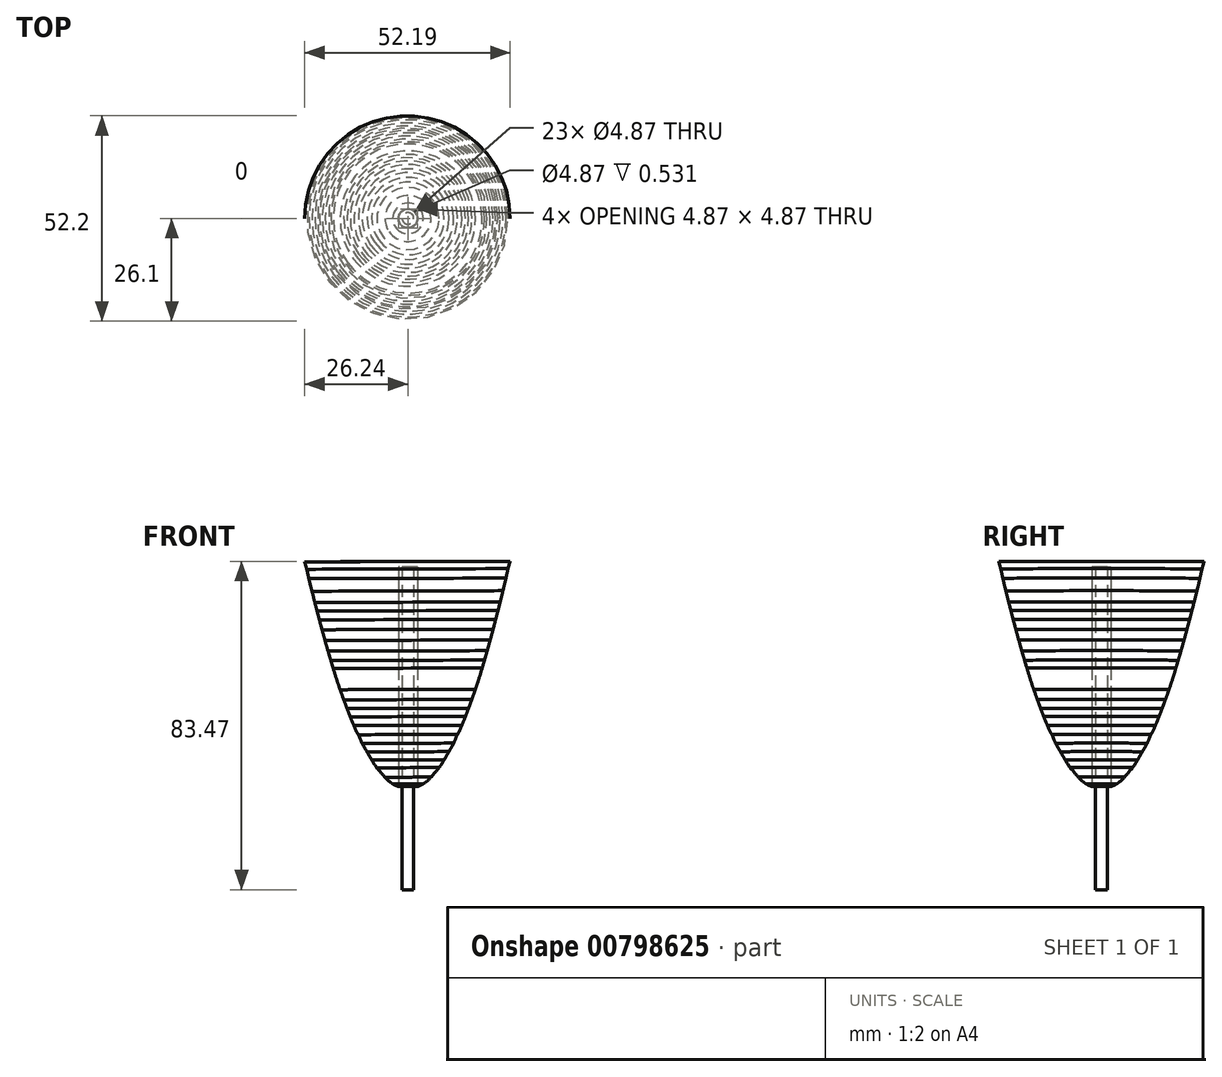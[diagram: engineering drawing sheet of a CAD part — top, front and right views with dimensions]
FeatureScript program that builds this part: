
annotation { "Feature Type Name" : "Feature", "Feature Type Description" : "" }
export const myFeature = defineFeature(function(context is Context, id is Id, definition is map)
    precondition{}
    {
        {
            var Q0;
            Q0=qCreatedBy(makeId("Front.planeOp"),FACE);
            var sketch = newSketch(context, id + "F0", { "sketchPlane" : qUnion([Q0])});
            skPoint(sketch, "E0", {"position": v(0.03, -0.02) * mm});
            skPoint(sketch, "E1", {"position": v(3.18, 1.13) * mm});
            skPoint(sketch, "E2", {"position": v(5.18, 2.5) * mm});
            skPoint(sketch, "E3", {"position": v(6.84, 4.37) * mm});
            skPoint(sketch, "E4", {"position": v(8.16, 5.94) * mm});
            skPoint(sketch, "E5", {"position": v(9.14, 7.52) * mm});
            skPoint(sketch, "E6", {"position": v(9.9, 8.84) * mm});
            skPoint(sketch, "E7", {"position": v(10.89, 10.54) * mm});
            skPoint(sketch, "E8", {"position": v(11.75, 12.1) * mm});
            skPoint(sketch, "E9", {"position": v(12.46, 13.83) * mm});
            skPoint(sketch, "E10", {"position": v(13.16, 15.1) * mm});
            skPoint(sketch, "E11", {"position": v(13.63, 16.27) * mm});
            skPoint(sketch, "E12", {"position": v(14.18, 17.52) * mm});
            skPoint(sketch, "E13", {"position": v(14.76, 19.04) * mm});
            skPoint(sketch, "E14", {"position": v(15.34, 20.55) * mm});
            skPoint(sketch, "E15", {"position": v(15.91, 22.07) * mm});
            skPoint(sketch, "E16", {"position": v(16.5, 23.66) * mm});
            skPoint(sketch, "E17", {"position": v(17, 25.39) * mm});
            skPoint(sketch, "E18", {"position": v(17.57, 26.83) * mm});
            skPoint(sketch, "E19", {"position": v(18.15, 28.78) * mm});
            skPoint(sketch, "E20", {"position": v(18.73, 30.87) * mm});
            skPoint(sketch, "E21", {"position": v(19.45, 32.97) * mm});
            skPoint(sketch, "E22", {"position": v(20.25, 35.58) * mm});
            skPoint(sketch, "E23", {"position": v(20.68, 37.74) * mm});
            skPoint(sketch, "E24", {"position": v(21.38, 39.85) * mm});
            skPoint(sketch, "E25", {"position": v(22, 42.1) * mm});
            skPoint(sketch, "E26", {"position": v(22.47, 44.2) * mm});
            skPoint(sketch, "E27", {"position": v(23.18, 47) * mm});
            skPoint(sketch, "E28", {"position": v(24.03, 50.12) * mm});
            skPoint(sketch, "E29", {"position": v(24.81, 53.4) * mm});
            skPoint(sketch, "E30", {"position": v(25.43, 56.2) * mm});
            skPoint(sketch, "E31", {"position": v(25.43, 58.07) * mm});
            skFitSpline(sketch, "E32", {"points": [v(0.03, -0.02) * mm, v(3.18, 1.13) * mm, v(5.18, 2.5) * mm, v(6.84, 4.37) * mm, v(8.16, 5.94) * mm, v(9.14, 7.52) * mm, v(9.9, 8.84) * mm, v(10.89, 10.54) * mm, v(11.75, 12.1) * mm, v(12.46, 13.83) * mm, v(13.16, 15.1) * mm, v(13.63, 16.27) * mm, v(14.18, 17.52) * mm, v(14.76, 19.04) * mm, v(15.34, 20.55) * mm, v(17.57, 26.83) * mm, v(19.45, 32.97) * mm, v(21.38, 39.85) * mm, v(24.81, 53.4) * mm, v(25.43, 56.2) * mm, v(25.95, 58.07) * mm], "startDerivative": vector(61.74, 19.66) * mm, "endDerivative": vector(13.33, 46) * mm});
            skLineSegment(sketch, "E33", {"start": v(25.95, 58.07) * mm, "end": v(-0.15, 58.07) * mm});
            skLineSegment(sketch, "E34", {"start": v(-0.15, 58.07) * mm, "end": v(0.03, -0.02) * mm});
            skLineSegment(sketch, "E35", {"start": v(19.45, 32.97) * mm, "end": v(-0.07, 32.97) * mm});
            skLineSegment(sketch, "E36", {"start": v(25.43, 56.2) * mm, "end": v(-0.14, 56.12) * mm});
            skLineSegment(sketch, "E37", {"start": v(23.97, 45.58) * mm, "end": v(-6.54, 45.48) * mm});
            skLineSegment(sketch, "E38", {"start": v(-4.68, 53.8) * mm, "end": v(34.04, 53.8) * mm});
            skLineSegment(sketch, "E39", {"start": v(-7.24, 50.6) * mm, "end": v(41.15, 50.6) * mm});
            skLineSegment(sketch, "E40", {"start": v(-7.24, 47.74) * mm, "end": v(38.8, 47.74) * mm});
            skLineSegment(sketch, "E41", {"start": v(-6.54, 43.31) * mm, "end": v(33.08, 43.31) * mm});
            skLineSegment(sketch, "E42", {"start": v(-6.61, 40.8) * mm, "end": v(35.36, 40.8) * mm});
            skLineSegment(sketch, "E43", {"start": v(-6.34, 38.08) * mm, "end": v(33.86, 38.08) * mm});
            skLineSegment(sketch, "E44", {"start": v(-4.24, 35.28) * mm, "end": v(35.36, 35.4) * mm});
            skLineSegment(sketch, "E45", {"start": v(-4.66, 30.97) * mm, "end": v(35.36, 30.97) * mm});
            skLineSegment(sketch, "E46", {"start": v(-4.61, 28.25) * mm, "end": v(32.86, 28.25) * mm});
            skLineSegment(sketch, "E47", {"start": v(-4.44, 25.54) * mm, "end": v(32.3, 25.54) * mm});
            skLineSegment(sketch, "E48", {"start": v(-4.61, 22.96) * mm, "end": v(29.5, 22.96) * mm});
            skLineSegment(sketch, "E49", {"start": v(-4.36, 20.74) * mm, "end": v(30.66, 20.74) * mm});
            skLineSegment(sketch, "E50", {"start": v(-4.32, 18.64) * mm, "end": v(26.14, 18.64) * mm});
            skLineSegment(sketch, "E51", {"start": v(-4.53, 16.42) * mm, "end": v(28.75, 16.42) * mm});
            skLineSegment(sketch, "E52", {"start": v(-4.37, 14.08) * mm, "end": v(25.46, 14.08) * mm});
            skLineSegment(sketch, "E53", {"start": v(-4.32, 11.86) * mm, "end": v(28.46, 11.86) * mm});
            skLineSegment(sketch, "E54", {"start": v(-4.25, 9.7) * mm, "end": v(25.28, 9.7) * mm});
            skLineSegment(sketch, "E55", {"start": v(-4.22, 7.66) * mm, "end": v(30.42, 7.66) * mm});
            skLineSegment(sketch, "E56", {"start": v(-4.18, 5.62) * mm, "end": v(24.54, 5.7) * mm});
            skLineSegment(sketch, "E57", {"start": v(-4.14, 3.23) * mm, "end": v(12.44, 3.23) * mm});
            skLineSegment(sketch, "E58", {"start": v(-4.34, 1.53) * mm, "end": v(8.85, 1.53) * mm});
            skSolve(sketch);
        }
        {
            var Q0;
            Q0=makeQuery(id+"F0.imprint","IMPRINT",FACE,{"disambiguationData":[TD([[makeQuery(id+"F0.imprint","IMPRINT",EDGE,{"derivedFrom":sQuery(id+"F0.wireOp",EDGE,"E32")}),1.0]])]});
            var Q1;
            Q1=sQuery(id+"F0.wireOp",EDGE,"E34");
            revolve(context, id + "F1", {"surfaceOperationType" : NewSurfaceOperationType.NEW, "entities" : qUnion([Q0]), "axis" : qUnion([Q1]), "revolveType" : RevolveType.FULL});
        }
        {
            var Q0;
            {var subQ0=sQuery(id+"F0.wireOp",EDGE,"E35");Q0=makeQuery(id+"F0.imprint","IMPRINT",FACE,{"disambiguationData":[TD([[makeQuery(id+"F0.imprint","IMPRINT",EDGE,{"derivedFrom":subQ0}),1.0]])]});}
            var Q1;
            Q1=sQuery(id+"F0.wireOp",EDGE,"E34");
            revolve(context, id + "F2", {"surfaceOperationType" : NewSurfaceOperationType.NEW, "entities" : qUnion([Q0]), "axis" : qUnion([Q1]), "revolveType" : RevolveType.FULL});
        }
        {
            var Q0;
            {var subQ0=sQuery(id+"F0.wireOp",EDGE,"E35");Q0=makeQuery(id+"F0.imprint","IMPRINT",FACE,{"disambiguationData":[TD([[makeQuery(id+"F0.imprint","IMPRINT",EDGE,{"derivedFrom":subQ0}),-1.0]])]});}
            var Q1;
            Q1=sQuery(id+"F0.wireOp",EDGE,"E34");
            revolve(context, id + "F3", {"surfaceOperationType" : NewSurfaceOperationType.NEW, "entities" : qUnion([Q0]), "axis" : qUnion([Q1]), "revolveType" : RevolveType.FULL});
        }
        {
            var Q0;
            {var subQ0=sQuery(id+"F0.wireOp",EDGE,"E36");Q0=makeQuery(id+"F0.imprint","IMPRINT",FACE,{"disambiguationData":[TD([[makeQuery(id+"F0.imprint","IMPRINT",EDGE,{"derivedFrom":subQ0}),1.0]])]});}
            var Q1;
            Q1=sQuery(id+"F0.wireOp",EDGE,"E34");
            revolve(context, id + "F4", {"surfaceOperationType" : NewSurfaceOperationType.NEW, "entities" : qUnion([Q0]), "axis" : qUnion([Q1]), "revolveType" : RevolveType.FULL});
        }
        {
            var Q0;
            {var subQ0=sQuery(id+"F0.wireOp",EDGE,"E33");Q0=makeQuery(id+"F0.imprint","IMPRINT",FACE,{"disambiguationData":[TD([[makeQuery(id+"F0.imprint","IMPRINT",EDGE,{"derivedFrom":subQ0}),1.0]])]});}
            var Q1;
            Q1=sQuery(id+"F0.wireOp",EDGE,"E34");
            revolve(context, id + "F5", {"surfaceOperationType" : NewSurfaceOperationType.NEW, "entities" : qUnion([Q0]), "axis" : qUnion([Q1]), "revolveType" : RevolveType.FULL});
        }
        {
            var Q0;
            {var subQ0=sQuery(id+"F0.wireOp",EDGE,"E39");var subQ1=sQuery(id+"F0.wireOp",EDGE,"E32");var subQ2=makeQuery(id+"F0.imprint","INTERSECT",VERTEX,{"derivedFrom":[subQ1,subQ0]});Q0=makeQuery(id+"F0.imprint","IMPRINT",FACE,{"disambiguationData":[TD([[makeQuery(id+"F0.imprint","IMPRINT",EDGE,{"disambiguationData":[TD([[subQ2,-1.0]])],"derivedFrom":subQ1}),1.0]])]});}
            var Q1;
            Q1=sQuery(id+"F0.wireOp",EDGE,"E34");
            revolve(context, id + "F6", {"surfaceOperationType" : NewSurfaceOperationType.NEW, "entities" : qUnion([Q0]), "axis" : qUnion([Q1]), "revolveType" : RevolveType.FULL});
        }
        {
            var Q0;
            {var subQ0=sQuery(id+"F0.wireOp",EDGE,"E40");var subQ1=sQuery(id+"F0.wireOp",EDGE,"E32");var subQ2=makeQuery(id+"F0.imprint","INTERSECT",VERTEX,{"derivedFrom":[subQ1,subQ0]});Q0=makeQuery(id+"F0.imprint","IMPRINT",FACE,{"disambiguationData":[TD([[makeQuery(id+"F0.imprint","IMPRINT",EDGE,{"disambiguationData":[TD([[subQ2,-1.0]])],"derivedFrom":subQ1}),1.0]])]});}
            var Q1;
            Q1=sQuery(id+"F0.wireOp",EDGE,"E34");
            revolve(context, id + "F7", {"surfaceOperationType" : NewSurfaceOperationType.NEW, "entities" : qUnion([Q0]), "axis" : qUnion([Q1]), "revolveType" : RevolveType.FULL});
        }
        {
            var Q0;
            {var subQ0=sQuery(id+"F0.wireOp",EDGE,"E37");var subQ1=sQuery(id+"F0.wireOp",EDGE,"E32");var subQ2=makeQuery(id+"F0.imprint","INTERSECT",VERTEX,{"derivedFrom":[subQ1,subQ0]});Q0=makeQuery(id+"F0.imprint","IMPRINT",FACE,{"disambiguationData":[TD([[makeQuery(id+"F0.imprint","IMPRINT",EDGE,{"disambiguationData":[TD([[subQ2,-1.0]])],"derivedFrom":subQ1}),1.0]])]});}
            var Q1;
            Q1=sQuery(id+"F0.wireOp",EDGE,"E34");
            revolve(context, id + "F8", {"surfaceOperationType" : NewSurfaceOperationType.NEW, "entities" : qUnion([Q0]), "axis" : qUnion([Q1]), "revolveType" : RevolveType.FULL});
        }
        {
            var Q0;
            {var subQ0=sQuery(id+"F0.wireOp",EDGE,"E41");var subQ1=sQuery(id+"F0.wireOp",EDGE,"E32");var subQ2=makeQuery(id+"F0.imprint","INTERSECT",VERTEX,{"derivedFrom":[subQ1,subQ0]});Q0=makeQuery(id+"F0.imprint","IMPRINT",FACE,{"disambiguationData":[TD([[makeQuery(id+"F0.imprint","IMPRINT",EDGE,{"disambiguationData":[TD([[subQ2,-1.0]])],"derivedFrom":subQ1}),1.0]])]});}
            var Q1;
            Q1=sQuery(id+"F0.wireOp",EDGE,"E34");
            revolve(context, id + "F9", {"surfaceOperationType" : NewSurfaceOperationType.NEW, "entities" : qUnion([Q0]), "axis" : qUnion([Q1]), "revolveType" : RevolveType.FULL});
        }
        {
            var Q0;
            {var subQ0=sQuery(id+"F0.wireOp",EDGE,"E42");var subQ1=sQuery(id+"F0.wireOp",EDGE,"E32");var subQ2=makeQuery(id+"F0.imprint","INTERSECT",VERTEX,{"derivedFrom":[subQ1,subQ0]});Q0=makeQuery(id+"F0.imprint","IMPRINT",FACE,{"disambiguationData":[TD([[makeQuery(id+"F0.imprint","IMPRINT",EDGE,{"disambiguationData":[TD([[subQ2,-1.0]])],"derivedFrom":subQ1}),1.0]])]});}
            var Q1;
            Q1=sQuery(id+"F0.wireOp",EDGE,"E34");
            revolve(context, id + "F10", {"surfaceOperationType" : NewSurfaceOperationType.NEW, "entities" : qUnion([Q0]), "axis" : qUnion([Q1]), "revolveType" : RevolveType.FULL});
        }
        {
            var Q0;
            {var subQ0=sQuery(id+"F0.wireOp",EDGE,"E43");var subQ1=sQuery(id+"F0.wireOp",EDGE,"E32");var subQ2=makeQuery(id+"F0.imprint","INTERSECT",VERTEX,{"derivedFrom":[subQ1,subQ0]});Q0=makeQuery(id+"F0.imprint","IMPRINT",FACE,{"disambiguationData":[TD([[makeQuery(id+"F0.imprint","IMPRINT",EDGE,{"disambiguationData":[TD([[subQ2,-1.0]])],"derivedFrom":subQ1}),1.0]])]});}
            var Q1;
            Q1=sQuery(id+"F0.wireOp",EDGE,"E34");
            revolve(context, id + "F11", {"surfaceOperationType" : NewSurfaceOperationType.NEW, "entities" : qUnion([Q0]), "axis" : qUnion([Q1]), "revolveType" : RevolveType.FULL});
        }
        {
            var Q0;
            {var subQ0=sQuery(id+"F0.wireOp",EDGE,"E44");var subQ1=sQuery(id+"F0.wireOp",EDGE,"E32");var subQ2=makeQuery(id+"F0.imprint","INTERSECT",VERTEX,{"derivedFrom":[subQ1,subQ0]});Q0=makeQuery(id+"F0.imprint","IMPRINT",FACE,{"disambiguationData":[TD([[makeQuery(id+"F0.imprint","IMPRINT",EDGE,{"disambiguationData":[TD([[subQ2,-1.0]])],"derivedFrom":subQ1}),1.0]])]});}
            var Q1;
            Q1=sQuery(id+"F0.wireOp",EDGE,"E34");
            revolve(context, id + "F12", {"surfaceOperationType" : NewSurfaceOperationType.NEW, "entities" : qUnion([Q0]), "axis" : qUnion([Q1]), "revolveType" : RevolveType.FULL});
        }
        {
            var Q0;
            {var subQ0=sQuery(id+"F0.wireOp",EDGE,"E46");var subQ1=sQuery(id+"F0.wireOp",EDGE,"E32");var subQ2=makeQuery(id+"F0.imprint","INTERSECT",VERTEX,{"derivedFrom":[subQ1,subQ0]});Q0=makeQuery(id+"F0.imprint","IMPRINT",FACE,{"disambiguationData":[TD([[makeQuery(id+"F0.imprint","IMPRINT",EDGE,{"disambiguationData":[TD([[subQ2,-1.0]])],"derivedFrom":subQ1}),1.0]])]});}
            var Q1;
            Q1=sQuery(id+"F0.wireOp",EDGE,"E34");
            revolve(context, id + "F13", {"surfaceOperationType" : NewSurfaceOperationType.NEW, "entities" : qUnion([Q0]), "axis" : qUnion([Q1]), "revolveType" : RevolveType.FULL});
        }
        {
            var Q0;
            {var subQ0=sQuery(id+"F0.wireOp",EDGE,"E47");var subQ1=sQuery(id+"F0.wireOp",EDGE,"E32");var subQ2=makeQuery(id+"F0.imprint","INTERSECT",VERTEX,{"derivedFrom":[subQ1,subQ0]});Q0=makeQuery(id+"F0.imprint","IMPRINT",FACE,{"disambiguationData":[TD([[makeQuery(id+"F0.imprint","IMPRINT",EDGE,{"disambiguationData":[TD([[subQ2,-1.0]])],"derivedFrom":subQ1}),1.0]])]});}
            var Q1;
            Q1=sQuery(id+"F0.wireOp",EDGE,"E34");
            revolve(context, id + "F14", {"operationType" : NewBodyOperationType.ADD, "surfaceOperationType" : NewSurfaceOperationType.NEW, "entities" : qUnion([Q0]), "axis" : qUnion([Q1]), "revolveType" : RevolveType.FULL});
        }
        {
            var Q0;
            {var subQ0=sQuery(id+"F0.wireOp",EDGE,"E48");var subQ1=sQuery(id+"F0.wireOp",EDGE,"E32");var subQ2=makeQuery(id+"F0.imprint","INTERSECT",VERTEX,{"derivedFrom":[subQ1,subQ0]});Q0=makeQuery(id+"F0.imprint","IMPRINT",FACE,{"disambiguationData":[TD([[makeQuery(id+"F0.imprint","IMPRINT",EDGE,{"disambiguationData":[TD([[subQ2,-1.0]])],"derivedFrom":subQ1}),1.0]])]});}
            var Q1;
            Q1=sQuery(id+"F0.wireOp",EDGE,"E34");
            revolve(context, id + "F15", {"surfaceOperationType" : NewSurfaceOperationType.NEW, "entities" : qUnion([Q0]), "axis" : qUnion([Q1]), "revolveType" : RevolveType.FULL});
        }
        {
            var Q0;
            {var subQ0=sQuery(id+"F0.wireOp",EDGE,"E49");var subQ1=sQuery(id+"F0.wireOp",EDGE,"E32");var subQ2=makeQuery(id+"F0.imprint","INTERSECT",VERTEX,{"derivedFrom":[subQ1,subQ0]});Q0=makeQuery(id+"F0.imprint","IMPRINT",FACE,{"disambiguationData":[TD([[makeQuery(id+"F0.imprint","IMPRINT",EDGE,{"disambiguationData":[TD([[subQ2,-1.0]])],"derivedFrom":subQ1}),1.0]])]});}
            var Q1;
            Q1=sQuery(id+"F0.wireOp",EDGE,"E34");
            revolve(context, id + "F16", {"surfaceOperationType" : NewSurfaceOperationType.NEW, "entities" : qUnion([Q0]), "axis" : qUnion([Q1]), "revolveType" : RevolveType.FULL});
        }
        {
            var Q0;
            {var subQ0=sQuery(id+"F0.wireOp",EDGE,"E50");var subQ1=sQuery(id+"F0.wireOp",EDGE,"E32");var subQ2=makeQuery(id+"F0.imprint","INTERSECT",VERTEX,{"derivedFrom":[subQ1,subQ0]});Q0=makeQuery(id+"F0.imprint","IMPRINT",FACE,{"disambiguationData":[TD([[makeQuery(id+"F0.imprint","IMPRINT",EDGE,{"disambiguationData":[TD([[subQ2,-1.0]])],"derivedFrom":subQ1}),1.0]])]});}
            var Q1;
            Q1=sQuery(id+"F0.wireOp",EDGE,"E34");
            revolve(context, id + "F17", {"surfaceOperationType" : NewSurfaceOperationType.NEW, "entities" : qUnion([Q0]), "axis" : qUnion([Q1]), "revolveType" : RevolveType.FULL});
        }
        {
            var Q0;
            {var subQ0=sQuery(id+"F0.wireOp",EDGE,"E51");var subQ1=sQuery(id+"F0.wireOp",EDGE,"E32");var subQ2=makeQuery(id+"F0.imprint","INTERSECT",VERTEX,{"derivedFrom":[subQ1,subQ0]});Q0=makeQuery(id+"F0.imprint","IMPRINT",FACE,{"disambiguationData":[TD([[makeQuery(id+"F0.imprint","IMPRINT",EDGE,{"disambiguationData":[TD([[subQ2,-1.0]])],"derivedFrom":subQ1}),1.0]])]});}
            var Q1;
            Q1=sQuery(id+"F0.wireOp",EDGE,"E34");
            revolve(context, id + "F18", {"surfaceOperationType" : NewSurfaceOperationType.NEW, "entities" : qUnion([Q0]), "axis" : qUnion([Q1]), "revolveType" : RevolveType.FULL});
        }
        {
            var Q0;
            {var subQ0=sQuery(id+"F0.wireOp",EDGE,"E52");var subQ1=sQuery(id+"F0.wireOp",EDGE,"E32");var subQ2=makeQuery(id+"F0.imprint","INTERSECT",VERTEX,{"derivedFrom":[subQ1,subQ0]});Q0=makeQuery(id+"F0.imprint","IMPRINT",FACE,{"disambiguationData":[TD([[makeQuery(id+"F0.imprint","IMPRINT",EDGE,{"disambiguationData":[TD([[subQ2,-1.0]])],"derivedFrom":subQ1}),1.0]])]});}
            var Q1;
            Q1=sQuery(id+"F0.wireOp",EDGE,"E34");
            revolve(context, id + "F19", {"surfaceOperationType" : NewSurfaceOperationType.NEW, "entities" : qUnion([Q0]), "axis" : qUnion([Q1]), "revolveType" : RevolveType.FULL});
        }
        {
            var Q0;
            {var subQ0=sQuery(id+"F0.wireOp",EDGE,"E53");var subQ1=sQuery(id+"F0.wireOp",EDGE,"E32");var subQ2=makeQuery(id+"F0.imprint","INTERSECT",VERTEX,{"derivedFrom":[subQ1,subQ0]});Q0=makeQuery(id+"F0.imprint","IMPRINT",FACE,{"disambiguationData":[TD([[makeQuery(id+"F0.imprint","IMPRINT",EDGE,{"disambiguationData":[TD([[subQ2,-1.0]])],"derivedFrom":subQ1}),1.0]])]});}
            var Q1;
            Q1=sQuery(id+"F0.wireOp",EDGE,"E34");
            revolve(context, id + "F20", {"surfaceOperationType" : NewSurfaceOperationType.NEW, "entities" : qUnion([Q0]), "axis" : qUnion([Q1]), "revolveType" : RevolveType.FULL});
        }
        {
            var Q0;
            {var subQ0=sQuery(id+"F0.wireOp",EDGE,"E54");var subQ1=sQuery(id+"F0.wireOp",EDGE,"E32");var subQ2=makeQuery(id+"F0.imprint","INTERSECT",VERTEX,{"derivedFrom":[subQ1,subQ0]});Q0=makeQuery(id+"F0.imprint","IMPRINT",FACE,{"disambiguationData":[TD([[makeQuery(id+"F0.imprint","IMPRINT",EDGE,{"disambiguationData":[TD([[subQ2,-1.0]])],"derivedFrom":subQ1}),1.0]])]});}
            var Q1;
            Q1=sQuery(id+"F0.wireOp",EDGE,"E34");
            revolve(context, id + "F21", {"surfaceOperationType" : NewSurfaceOperationType.NEW, "entities" : qUnion([Q0]), "axis" : qUnion([Q1]), "revolveType" : RevolveType.FULL});
        }
        {
            var Q0;
            {var subQ0=sQuery(id+"F0.wireOp",EDGE,"E55");var subQ1=sQuery(id+"F0.wireOp",EDGE,"E32");var subQ2=makeQuery(id+"F0.imprint","INTERSECT",VERTEX,{"derivedFrom":[subQ1,subQ0]});Q0=makeQuery(id+"F0.imprint","IMPRINT",FACE,{"disambiguationData":[TD([[makeQuery(id+"F0.imprint","IMPRINT",EDGE,{"disambiguationData":[TD([[subQ2,-1.0]])],"derivedFrom":subQ1}),1.0]])]});}
            var Q1;
            Q1=sQuery(id+"F0.wireOp",EDGE,"E34");
            revolve(context, id + "F22", {"surfaceOperationType" : NewSurfaceOperationType.NEW, "entities" : qUnion([Q0]), "axis" : qUnion([Q1]), "revolveType" : RevolveType.FULL});
        }
        {
            var Q0;
            {var subQ0=sQuery(id+"F0.wireOp",EDGE,"E56");var subQ1=sQuery(id+"F0.wireOp",EDGE,"E32");var subQ2=makeQuery(id+"F0.imprint","INTERSECT",VERTEX,{"derivedFrom":[subQ1,subQ0]});Q0=makeQuery(id+"F0.imprint","IMPRINT",FACE,{"disambiguationData":[TD([[makeQuery(id+"F0.imprint","IMPRINT",EDGE,{"disambiguationData":[TD([[subQ2,-1.0]])],"derivedFrom":subQ1}),1.0]])]});}
            var Q1;
            Q1=sQuery(id+"F0.wireOp",EDGE,"E34");
            revolve(context, id + "F23", {"surfaceOperationType" : NewSurfaceOperationType.NEW, "entities" : qUnion([Q0]), "axis" : qUnion([Q1]), "revolveType" : RevolveType.FULL});
        }
        {
            var Q0;
            {var subQ0=sQuery(id+"F0.wireOp",EDGE,"E57");var subQ1=sQuery(id+"F0.wireOp",EDGE,"E32");var subQ2=makeQuery(id+"F0.imprint","INTERSECT",VERTEX,{"derivedFrom":[subQ1,subQ0]});Q0=makeQuery(id+"F0.imprint","IMPRINT",FACE,{"disambiguationData":[TD([[makeQuery(id+"F0.imprint","IMPRINT",EDGE,{"disambiguationData":[TD([[subQ2,-1.0]])],"derivedFrom":subQ1}),1.0]])]});}
            var Q1;
            Q1=sQuery(id+"F0.wireOp",EDGE,"E34");
            revolve(context, id + "F24", {"surfaceOperationType" : NewSurfaceOperationType.NEW, "entities" : qUnion([Q0]), "axis" : qUnion([Q1]), "revolveType" : RevolveType.FULL});
        }
        {
            var Q0;
            {var subQ0=sQuery(id+"F0.wireOp",EDGE,"E58");var subQ1=sQuery(id+"F0.wireOp",EDGE,"E32");var subQ2=makeQuery(id+"F0.imprint","INTERSECT",VERTEX,{"derivedFrom":[subQ1,subQ0]});Q0=makeQuery(id+"F0.imprint","IMPRINT",FACE,{"disambiguationData":[TD([[makeQuery(id+"F0.imprint","IMPRINT",EDGE,{"disambiguationData":[TD([[subQ2,-1.0]])],"derivedFrom":subQ1}),1.0]])]});}
            var Q1;
            Q1=sQuery(id+"F0.wireOp",EDGE,"E34");
            revolve(context, id + "F25", {"surfaceOperationType" : NewSurfaceOperationType.NEW, "entities" : qUnion([Q0]), "axis" : qUnion([Q1]), "revolveType" : RevolveType.FULL});
        }
        {
            var Q0;
            Q0=qCreatedBy(makeId("Top.planeOp"),FACE);
            var sketch = newSketch(context, id + "F26", { "sketchPlane" : qUnion([Q0])});
            skCircle(sketch, "E59", {"center": v(0, 0) * mm, "radius": 2.44 * mm});
            skSolve(sketch);
        }
        {
            var Q0;
            Q0=makeQuery(id+"F26.imprint","IMPRINT",FACE,{"disambiguationData":[TD([[makeQuery(id+"F26.imprint","IMPRINT",EDGE,{"derivedFrom":sQuery(id+"F26.wireOp",EDGE,"E59")}),1.0]])]});
            extrude(context, id + "F27", {"entities" : qUnion([Q0]), "operationType" : NewBodyOperationType.REMOVE, "depth" : 56.64 * mm, "offsetDistance" : 25.4 * mm});
        }
        {
            var Q0;
            Q0=qCreatedBy(makeId("Top.planeOp"),FACE);
            var sketch = newSketch(context, id + "F28", { "sketchPlane" : qUnion([Q0])});
            skCircle(sketch, "E60", {"center": v(0, 0) * mm, "radius": 1.48 * mm});
            skSolve(sketch);
        }
        {
            var Q0;
            Q0=makeQuery(id+"F28.imprint","IMPRINT",FACE,{"disambiguationData":[TD([[makeQuery(id+"F28.imprint","IMPRINT",EDGE,{"derivedFrom":sQuery(id+"F28.wireOp",EDGE,"E60")}),1.0]])]});
            var Q1;
            Q1=sQuery(id+"F28.wireOp",EDGE,"E60");
            extrude(context, id + "F29", {"entities" : qUnion([Q0]), "operationType" : NewBodyOperationType.ADD, "surfaceEntities" : qUnion([Q1]), "depth" : 57.66 * mm, "offsetDistance" : 25.4 * mm});
        }
        {
            var Q0;
            Q0=makeQuery(id+"F29.opExtrude","CAP_FACE",FACE,{"disambiguationData":[OSD([sQuery(id+"F28.wireOp",EDGE,"E60")])],"isStart":true});
            cPlane(context, id + "F30", {"entities" : qUnion([Q0]), "cplaneType" : CPlaneType.OFFSET, "offset" : 25.4 * mm, "width" : 152.4 * mm, "height" : 152.4 * mm});
        }
        {
            var Q0;
            Q0=qCreatedBy(id+"F30.planeOp",FACE);
            var sketch = newSketch(context, id + "F31", { "sketchPlane" : qUnion([Q0])});
            skCircle(sketch, "E61", {"center": v(0, 0) * mm, "radius": 1.48 * mm});
            skSolve(sketch);
        }
        {
            var Q0;
            Q0=qSketchRegion(id+"F31",true);
            extrude(context, id + "F32", {"entities" : qUnion([Q0]), "operationType" : NewBodyOperationType.ADD, "oppositeDirection" : true, "depth" : 33.02 * mm, "offsetDistance" : 25.4 * mm});
        }
    });
